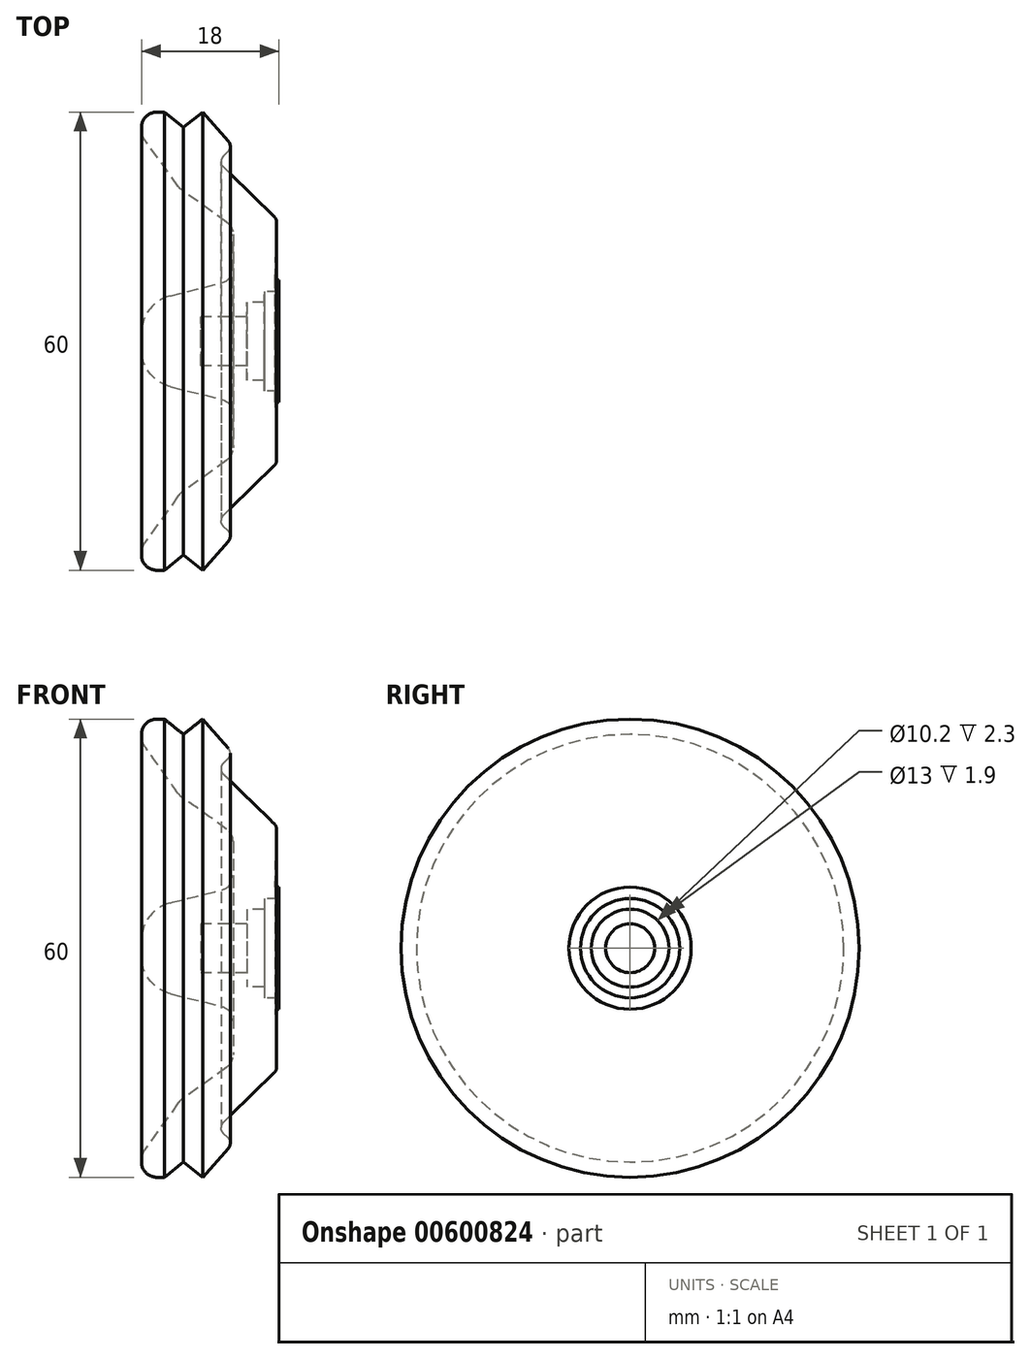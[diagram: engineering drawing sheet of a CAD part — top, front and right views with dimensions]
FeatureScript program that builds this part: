
annotation { "Feature Type Name" : "Feature", "Feature Type Description" : "" }
export const myFeature = defineFeature(function(context is Context, id is Id, definition is map)
    precondition{}
    {
        {
            var Q0;
            Q0=qCreatedBy(makeId("Front.planeOp"),FACE);
            var sketch = newSketch(context, id + "F0", { "sketchPlane" : qUnion([Q0])});
            skLineSegment(sketch, "E0", {"start": v(7.8, 0) * mm, "end": v(7.8, 3.2) * mm});
            skLineSegment(sketch, "E1", {"start": v(7.8, 3.2) * mm, "end": v(13.8, 3.2) * mm});
            skLineSegment(sketch, "E2", {"start": v(13.8, 3.2) * mm, "end": v(13.8, 5.1) * mm});
            skLineSegment(sketch, "E3", {"start": v(13.8, 5.1) * mm, "end": v(16.1, 5.1) * mm});
            skLineSegment(sketch, "E4", {"start": v(16.1, 5.1) * mm, "end": v(16.1, 6.5) * mm});
            skLineSegment(sketch, "E5", {"start": v(16.1, 6.5) * mm, "end": v(18, 6.5) * mm});
            skLineSegment(sketch, "E6", {"start": v(12, 9.56) * mm, "end": v(12, 13.97) * mm});
            skLineSegment(sketch, "E7", {"start": v(11.16, 15.6) * mm, "end": v(5.27, 19.8) * mm});
            skLineSegment(sketch, "E8", {"start": v(2, 30) * mm, "end": v(3, 30) * mm});
            skLineSegment(sketch, "E9", {"start": v(11.33, 24.83) * mm, "end": v(10.72, 24.22) * mm});
            skLineSegment(sketch, "E10", {"start": v(10.73, 22.8) * mm, "end": v(17.39, 16.3) * mm});
            skLineSegment(sketch, "E11", {"start": v(17.69, 15.56) * mm, "end": v(17.5, 8) * mm});
            skLineSegment(sketch, "E12", {"start": v(17.5, 8) * mm, "end": v(18, 8) * mm});
            skLineSegment(sketch, "E13", {"start": v(18, 8) * mm, "end": v(18, 6.5) * mm});
            skLineSegment(sketch, "E14", {"start": v(8, 30) * mm, "end": v(5.5, 28) * mm});
            skLineSegment(sketch, "E15", {"start": v(5.5, 28) * mm, "end": v(3, 30) * mm});
            skLineSegment(sketch, "E16", {"start": v(4.8, 20.27) * mm, "end": v(0.37, 26.48) * mm});
            skLineSegment(sketch, "E17", {"start": v(0, 27.64) * mm, "end": v(0, 28) * mm});
            skLineSegment(sketch, "E18", {"start": v(8, 30) * mm, "end": v(11.37, 26.2) * mm});
            skPoint(sketch, "E19.visualSharp", {"position": v(17.7, 16) * mm});
            skArc(sketch, "E19.filletArc", {"start": v(17.69, 15.56) * mm, "mid": v(17.62, 15.97) * mm, "end": v(17.39, 16.3) * mm});
            skPoint(sketch, "E20.visualSharp", {"position": v(0, 30) * mm});
            skArc(sketch, "E20.filletArc", {"start": v(2, 30) * mm, "mid": v(0.59, 29.41) * mm, "end": v(0, 28) * mm});
            skPoint(sketch, "E21.visualSharp", {"position": v(12, 25.5) * mm});
            skArc(sketch, "E21.filletArc", {"start": v(11.33, 24.83) * mm, "mid": v(11.63, 25.51) * mm, "end": v(11.37, 26.2) * mm});
            skPoint(sketch, "E22.visualSharp", {"position": v(10, 23.5) * mm});
            skArc(sketch, "E22.filletArc", {"start": v(10.72, 24.22) * mm, "mid": v(10.42, 23.5) * mm, "end": v(10.73, 22.8) * mm});
            skPoint(sketch, "E23.visualSharp", {"position": v(0, 27) * mm});
            skArc(sketch, "E23.filletArc", {"start": v(0, 27.64) * mm, "mid": v(0.1, 27.03) * mm, "end": v(0.37, 26.48) * mm});
            skPoint(sketch, "E24.visualSharp", {"position": v(5, 20) * mm});
            skArc(sketch, "E24.filletArc", {"start": v(4.8, 20.27) * mm, "mid": v(5.02, 20.02) * mm, "end": v(5.27, 19.8) * mm});
            skPoint(sketch, "E25.visualSharp", {"position": v(12, 8) * mm});
            skPoint(sketch, "E26.visualSharp", {"position": v(12, 15) * mm});
            skArc(sketch, "E26.filletArc", {"start": v(12, 13.97) * mm, "mid": v(11.78, 14.89) * mm, "end": v(11.16, 15.6) * mm});
            skPoint(sketch, "E27.visualSharp", {"position": v(0, 5) * mm});
            skLineSegment(sketch, "E28", {"start": v(0, 0) * mm, "end": v(7.8, 0) * mm});
            skLineSegment(sketch, "E29", {"start": v(10.49, 7.62) * mm, "end": v(3.79, 5.95) * mm});
            skLineSegment(sketch, "E30", {"start": v(0, 0) * mm, "end": v(0, 1.1) * mm});
            skArc(sketch, "E31.filletArc", {"start": v(3.79, 5.95) * mm, "mid": v(1.06, 4.17) * mm, "end": v(0, 1.1) * mm});
            skArc(sketch, "E32.filletArc", {"start": v(10.49, 7.62) * mm, "mid": v(11.58, 8.33) * mm, "end": v(12, 9.56) * mm});
            skSolve(sketch);
        }
        {
            var Q0;
            Q0=makeQuery(id+"F0.imprint","IMPRINT",FACE,{"disambiguationData":[TD([[makeQuery(id+"F0.imprint","IMPRINT",EDGE,{"derivedFrom":sQuery(id+"F0.wireOp",EDGE,"E0")}),1.0]])]});
            var Q1;
            Q1=sQuery(id+"F0.wireOp",EDGE,"E28");
            revolve(context, id + "F1", {"surfaceOperationType" : NewSurfaceOperationType.NEW, "entities" : qUnion([Q0]), "axis" : qUnion([Q1]), "revolveType" : RevolveType.FULL});
        }
    });
